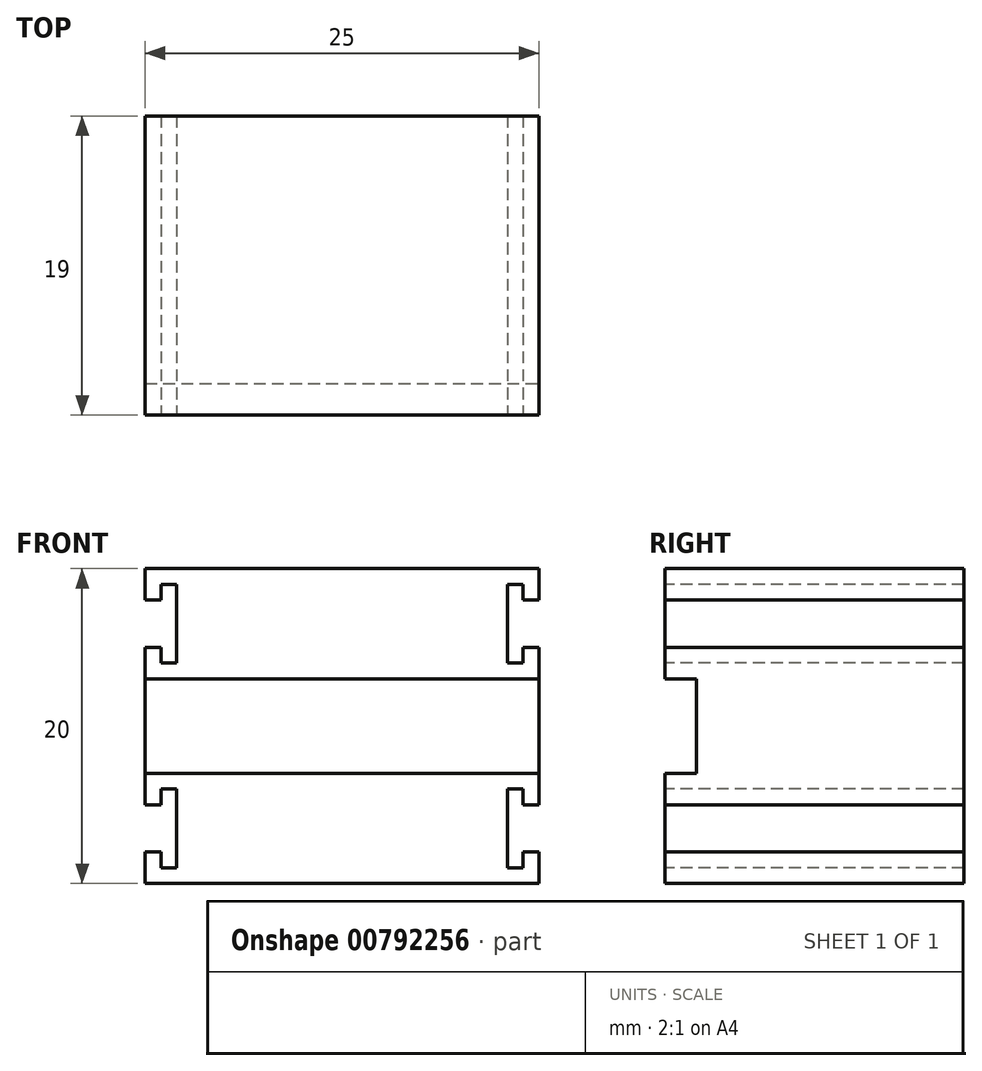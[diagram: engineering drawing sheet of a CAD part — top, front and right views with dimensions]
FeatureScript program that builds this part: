
annotation { "Feature Type Name" : "Feature", "Feature Type Description" : "" }
export const myFeature = defineFeature(function(context is Context, id is Id, definition is map)
    precondition{}
    {
        {
            var Q0;
            Q0=qCreatedBy(makeId("Front.planeOp"),FACE);
            var sketch = newSketch(context, id + "F0", { "sketchPlane" : qUnion([Q0])});
            skLineSegment(sketch, "E0.bottom", {"start": v(12.5, -10) * mm, "end": v(-12.5, -10) * mm});
            skLineSegment(sketch, "E0.top", {"start": v(12.5, 10) * mm, "end": v(-12.5, 10) * mm});
            skLineSegment(sketch, "E0.left", {"start": v(12.5, -10) * mm, "end": v(12.5, 10) * mm});
            skLineSegment(sketch, "E0.right", {"start": v(-12.5, -10) * mm, "end": v(-12.5, 10) * mm});
            skPoint(sketch, "E0.middle", {"position": v(0, 0) * mm});
            skSolve(sketch);
        }
        {
            var Q0;
            Q0 = qSketchRegion(id + "F0", true);
            extrude(context, id + "F1", {"entities" : qUnion([Q0]), "oppositeDirection" : true, "depth" : 19 * mm, "offsetDistance" : 25 * mm});
        }
        {
            var Q0;
            Q0=makeQuery(id+"F1.opExtrude","CAP_FACE",FACE,{"disambiguationData":[OSD([sQuery(id+"F0.wireOp",EDGE,"E0.bottom"),sQuery(id+"F0.wireOp",EDGE,"E0.top"),sQuery(id+"F0.wireOp",EDGE,"E0.left"),sQuery(id+"F0.wireOp",EDGE,"E0.right")])],"isStart":true});
            var sketch = newSketch(context, id + "F2", { "sketchPlane" : qUnion([Q0])});
            skLineSegment(sketch, "E1.bottom", {"start": v(-12.5, 3) * mm, "end": v(12.5, 3) * mm});
            skLineSegment(sketch, "E1.top", {"start": v(-12.5, -3) * mm, "end": v(12.5, -3) * mm});
            skLineSegment(sketch, "E1.left", {"start": v(-12.5, 3) * mm, "end": v(-12.5, -3) * mm});
            skLineSegment(sketch, "E1.right", {"start": v(12.5, 3) * mm, "end": v(12.5, -3) * mm});
            skSolve(sketch);
        }
        {
            var Q0;
            Q0 = qSketchRegion(id + "F2", true);
            extrude(context, id + "F3", {"entities" : qUnion([Q0]), "operationType" : NewBodyOperationType.REMOVE, "oppositeDirection" : true, "depth" : 2 * mm, "offsetDistance" : 25 * mm});
        }
        {
            var Q0;
            {var subQ0=sQuery(id+"F0.wireOp",EDGE,"E0.top");var subQ1=sQuery(id+"F0.wireOp",EDGE,"E0.left");var subQ2=sQuery(id+"F0.wireOp",EDGE,"E0.right");Q0=makeQuery(id+"F3.boolean.opBoolean","SPLIT",FACE,{"disambiguationData":[TD([makeQuery(id+"F1.opExtrude","SWEPT_FACE",FACE,{"disambiguationData":[OSD([subQ0])]})])],"derivedFrom":makeQuery(id+"F1.opExtrude","CAP_FACE",FACE,{"disambiguationData":[OSD([sQuery(id+"F0.wireOp",EDGE,"E0.bottom"),subQ0,subQ1,subQ2])],"isStart":true})});}
            var sketch = newSketch(context, id + "F4", { "sketchPlane" : qUnion([Q0])});
            skLineSegment(sketch, "E2", {"start": v(-12.5, 8) * mm, "end": v(-11.5, 8) * mm});
            skLineSegment(sketch, "E3", {"start": v(-11.5, 8) * mm, "end": v(-11.5, 9) * mm});
            skLineSegment(sketch, "E4", {"start": v(-11.5, 9) * mm, "end": v(-10.5, 9) * mm});
            skLineSegment(sketch, "E5", {"start": v(-10.5, 9) * mm, "end": v(-10.5, 4) * mm});
            skLineSegment(sketch, "E6", {"start": v(-10.5, 4) * mm, "end": v(-11.5, 4) * mm});
            skLineSegment(sketch, "E7", {"start": v(-11.5, 4) * mm, "end": v(-11.5, 5) * mm});
            skLineSegment(sketch, "E8", {"start": v(-11.5, 5) * mm, "end": v(-12.5, 5) * mm});
            skLineSegment(sketch, "E9", {"start": v(-12.5, 5) * mm, "end": v(-12.5, 8) * mm});
            skLineSegment(sketch, "E10", {"start": v(0, 10) * mm, "end": v(0, -10.04) * mm, "construction": true});
            skLineSegment(sketch, "E11.MirrorCS", {"start": v(11.5, 9) * mm, "end": v(10.5, 9) * mm});
            skLineSegment(sketch, "E12.MirrorCS", {"start": v(10.5, 4) * mm, "end": v(11.5, 4) * mm});
            skLineSegment(sketch, "E13.MirrorCS", {"start": v(12.5, 8) * mm, "end": v(11.5, 8) * mm});
            skLineSegment(sketch, "E14.MirrorCS", {"start": v(11.5, 5) * mm, "end": v(12.5, 5) * mm});
            skLineSegment(sketch, "E15.MirrorCS", {"start": v(11.5, 4) * mm, "end": v(11.5, 5) * mm});
            skLineSegment(sketch, "E16.MirrorCS", {"start": v(10.5, 9) * mm, "end": v(10.5, 4) * mm});
            skLineSegment(sketch, "E17.MirrorCS", {"start": v(11.5, 8) * mm, "end": v(11.5, 9) * mm});
            skLineSegment(sketch, "E18.MirrorCS", {"start": v(12.5, 5) * mm, "end": v(12.5, 8) * mm});
            skLineSegment(sketch, "E19", {"start": v(-12.98, 0) * mm, "end": v(13.94, 0) * mm, "construction": true});
            skLineSegment(sketch, "E20.MirrorCS", {"start": v(-11.5, -5) * mm, "end": v(-12.5, -5) * mm});
            skLineSegment(sketch, "E21.MirrorCS", {"start": v(11.5, -5) * mm, "end": v(12.5, -5) * mm});
            skLineSegment(sketch, "E22.MirrorCS", {"start": v(-12.5, -8) * mm, "end": v(-11.5, -8) * mm});
            skLineSegment(sketch, "E23.MirrorCS", {"start": v(-10.5, -4) * mm, "end": v(-11.5, -4) * mm});
            skLineSegment(sketch, "E24.MirrorCS", {"start": v(11.5, -9) * mm, "end": v(10.5, -9) * mm});
            skLineSegment(sketch, "E25.MirrorCS", {"start": v(-11.5, -9) * mm, "end": v(-10.5, -9) * mm});
            skLineSegment(sketch, "E26.MirrorCS", {"start": v(10.5, -4) * mm, "end": v(11.5, -4) * mm});
            skLineSegment(sketch, "E27.MirrorCS", {"start": v(12.5, -8) * mm, "end": v(11.5, -8) * mm});
            skLineSegment(sketch, "E28.MirrorCS", {"start": v(10.5, -9) * mm, "end": v(10.5, -4) * mm});
            skLineSegment(sketch, "E29.MirrorCS", {"start": v(-10.5, -9) * mm, "end": v(-10.5, -4) * mm});
            skLineSegment(sketch, "E30.MirrorCS", {"start": v(-11.5, -4) * mm, "end": v(-11.5, -5) * mm});
            skLineSegment(sketch, "E31.MirrorCS", {"start": v(11.5, -8) * mm, "end": v(11.5, -9) * mm});
            skLineSegment(sketch, "E32.MirrorCS", {"start": v(-12.5, -5) * mm, "end": v(-12.5, -8) * mm});
            skLineSegment(sketch, "E33.MirrorCS", {"start": v(12.5, -5) * mm, "end": v(12.5, -8) * mm});
            skLineSegment(sketch, "E34.MirrorCS", {"start": v(-11.5, -8) * mm, "end": v(-11.5, -9) * mm});
            skLineSegment(sketch, "E35.MirrorCS", {"start": v(11.5, -4) * mm, "end": v(11.5, -5) * mm});
            skSolve(sketch);
        }
        {
            var Q0;
            Q0 = qSketchRegion(id + "F4", true);
            extrude(context, id + "F5", {"entities" : qUnion([Q0]), "operationType" : NewBodyOperationType.REMOVE, "endBound" : BoundingType.THROUGH_ALL, "oppositeDirection" : true, "depth" : 25 * mm, "offsetDistance" : 25 * mm});
        }
    });
